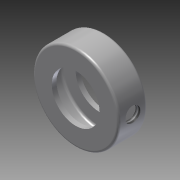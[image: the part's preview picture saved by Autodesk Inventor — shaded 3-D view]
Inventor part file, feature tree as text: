
AUTODESK INVENTOR PART (.ipt)
format: ipt  version: 2014 (Build 180170000, 170)  size: 169,472 bytes
history: native  units: in
note: dims shown in document units (in); Inventor stores cm internally (conversion verified against a paired STEP export)
features: sketch x4, extrude x2, fillet x1, revolve x1, plane x1, hole x1
ambient origin geometry x8: Origin, YZ Plane, XZ Plane, XY Plane, X Axis, Y Axis, Z Axis, Center Point
bodies: Solid1 (feature_tree)
feature tree (10):
  extrude  "Extrusion1"  Depth=0.0312in TaperAngle=0.0deg
  fillet  "Fillet1"  Radius=0.0312in
  extrude  "Extrusion2"  Depth=0.375in TaperAngle=0.0deg
  revolve  "Revolution1"  [1 undecoded]
  plane  "Work Plane1"
  hole  "Hole1"  [1 undecoded]
  sketch  "Sketch1"  dims[d0=1.125in d1=0.375in d2=0.0in d3=0.0312in]
  sketch  "Sketch2"  dims[d4=0.625in d5=0.375in d6=0.0in]
  sketch  "Sketch3"  dims[d7=0.0625in d8=0.0625in]
  sketch  "Sketch4"  dims[d9=0.0625in d10=0.0312in d11=90.0deg d12=0.196in d13=0.75in d14=0.375in d15=0.25in d16=0.5635in d17=1.0in d18=0.8108in]
note: 2 required parameter values undecoded (feature->parameter linkage not recoverable at this tier; creation-order binding heuristic only, values carry confidence <= 0.55)